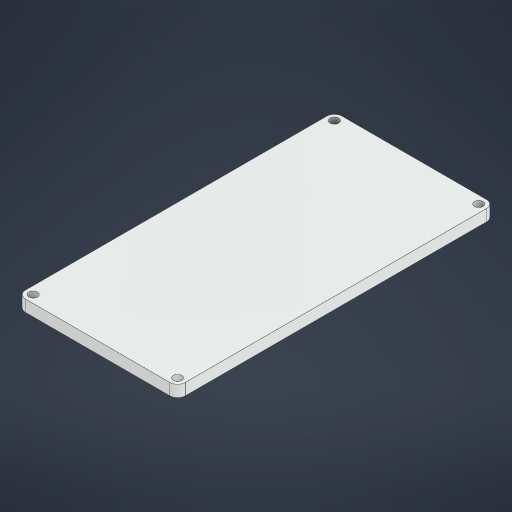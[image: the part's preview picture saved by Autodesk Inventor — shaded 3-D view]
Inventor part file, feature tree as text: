
AUTODESK INVENTOR PART (.ipt)
format: ipt  version: 2024.2 (Build 282272000, 272)  size: 188,928 bytes
history: native  units: mm
features: other x2, extrude x1, sketch x1
ambient origin geometry x8: Origin, YZ Plane, XZ Plane, XY Plane, X Axis, Y Axis, Z Axis, Center Point
bodies: Solid1 (feature_tree)
feature tree (4):
  extrude  "Extrusion1"  Depth=82.0mm
  sketch  "Sketch1"  dims[d0=41.392mm d1=82.0mm d2=2.0mm d3=2.2mm d5=2.006mm d6=2.006mm d7=2.2mm d8=2.006mm d9=2.006mm d10=2.2mm d11=2.006mm d12=2.006mm d13=2.2mm d14=2.006mm d15=2.006mm d16=37.386mm d17=3.0mm d18=0.0mm]
  other  "Finish1"
  other  "Finish2"
